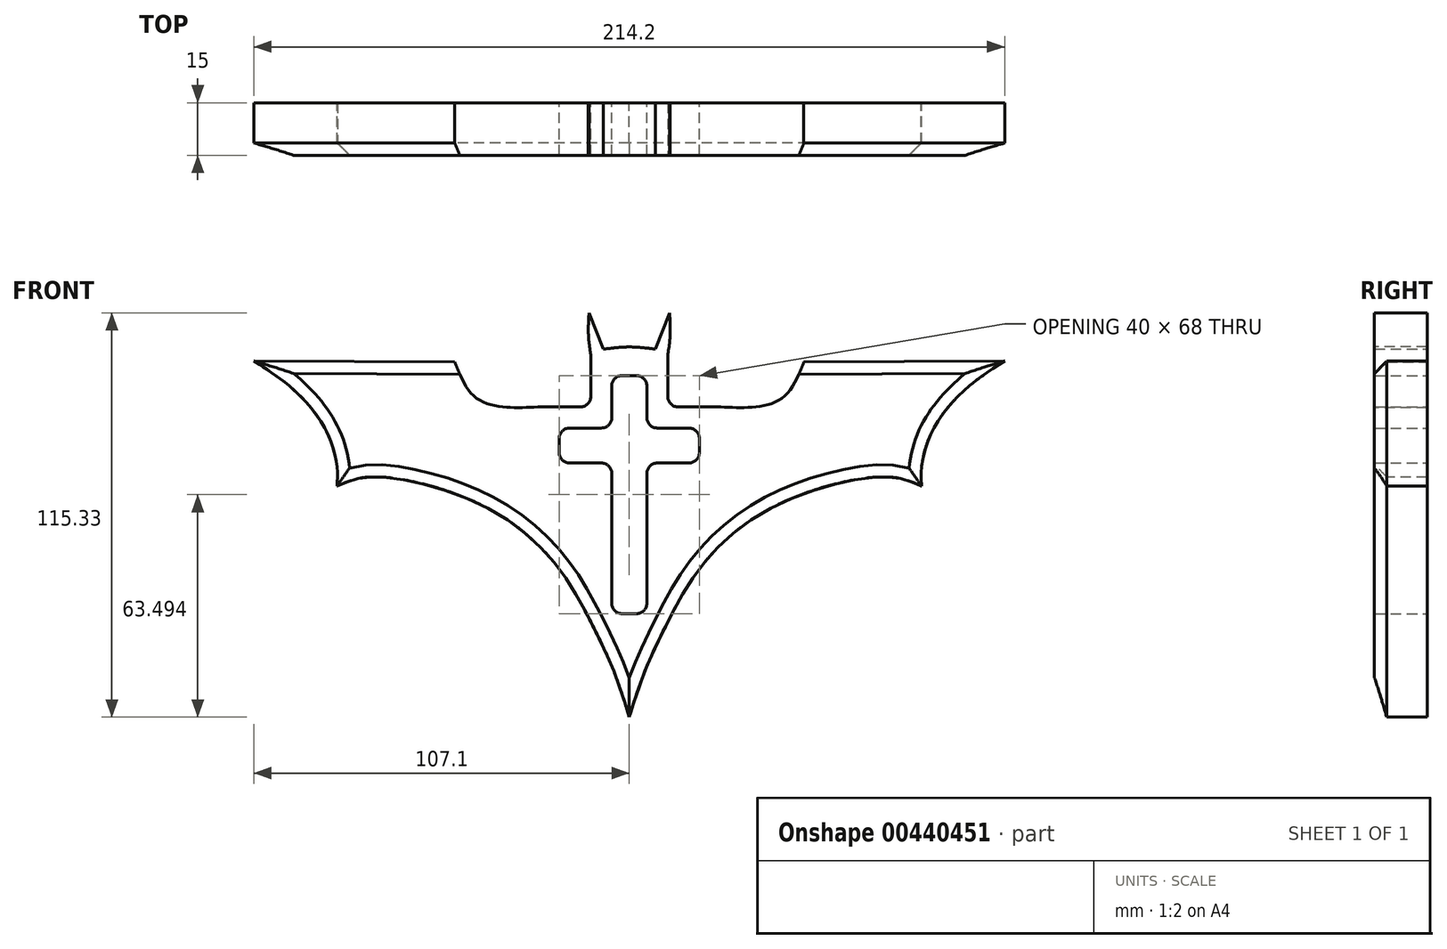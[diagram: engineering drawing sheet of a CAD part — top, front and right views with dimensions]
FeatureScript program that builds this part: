
annotation { "Feature Type Name" : "Feature", "Feature Type Description" : "" }
export const myFeature = defineFeature(function(context is Context, id is Id, definition is map)
    precondition{}
    {
        {
            var Q0;
            Q0=qCreatedBy(makeId("Front.planeOp"),FACE);
            var sketch = newSketch(context, id + "F0", { "sketchPlane" : qUnion([Q0])});
            skLineSegment(sketch, "E0", {"start": v(0, 58.13) * mm, "end": v(-10, 58.13) * mm});
            skLineSegment(sketch, "E1", {"start": v(-10, 58.13) * mm, "end": v(-10, 43.13) * mm});
            skLineSegment(sketch, "E2", {"start": v(-10, 43.13) * mm, "end": v(-25, 43.13) * mm});
            skLineSegment(sketch, "E3", {"start": v(-25, 43.13) * mm, "end": v(-25, 33.13) * mm});
            skLineSegment(sketch, "E4", {"start": v(-25, 33.13) * mm, "end": v(-10, 33.13) * mm});
            skLineSegment(sketch, "E5", {"start": v(0, 43.13) * mm, "end": v(15, 43.13) * mm});
            skLineSegment(sketch, "E6", {"start": v(0, 33.13) * mm, "end": v(15, 33.13) * mm});
            skLineSegment(sketch, "E7", {"start": v(15, 43.13) * mm, "end": v(15, 33.13) * mm});
            skLineSegment(sketch, "E8", {"start": v(0, 58.13) * mm, "end": v(0, 43.13) * mm});
            skLineSegment(sketch, "E9", {"start": v(-25, 27.13) * mm, "end": v(-16, 27.13) * mm});
            skLineSegment(sketch, "E10", {"start": v(6, 27.13) * mm, "end": v(15, 27.13) * mm});
            skLineSegment(sketch, "E11", {"start": v(15, 27.13) * mm, "end": v(21, 27.13) * mm});
            skLineSegment(sketch, "E12", {"start": v(21, 49.13) * mm, "end": v(6, 49.13) * mm});
            skLineSegment(sketch, "E13", {"start": v(6, 49.13) * mm, "end": v(6, 64.13) * mm});
            skLineSegment(sketch, "E14", {"start": v(6, 64.13) * mm, "end": v(-16, 64.13) * mm});
            skLineSegment(sketch, "E15", {"start": v(-16, 64.13) * mm, "end": v(-16, 49.13) * mm});
            skLineSegment(sketch, "E16", {"start": v(-16, 49.13) * mm, "end": v(-31, 49.13) * mm});
            skLineSegment(sketch, "E17", {"start": v(-31, 27.13) * mm, "end": v(-25, 27.13) * mm});
            skLineSegment(sketch, "E18", {"start": v(-16, 64.13) * mm, "end": v(-5, 64.13) * mm});
            skLineSegment(sketch, "E19", {"start": v(-5, 64.13) * mm, "end": v(-5, -22.87) * mm, "construction": true});
            skLineSegment(sketch, "E20", {"start": v(-31, 49.13) * mm, "end": v(-31, 27.13) * mm});
            skLineSegment(sketch, "E21", {"start": v(21, 49.13) * mm, "end": v(21, 27.13) * mm});
            skPoint(sketch, "E22", {"position": v(-88.4, 26.55) * mm});
            skFitSpline(sketch, "E23", {"points": [v(-31, 49.13) * mm, v(-40.4, 49.13) * mm, v(-49.1, 52.05) * mm, v(-54.8, 61.95) * mm], "startDerivative": vector(-28.83, -1.26) * mm, "endDerivative": vector(-12.96, 32.34) * mm});
            skPoint(sketch, "E24", {"position": v(-112.1, 62.25) * mm});
            skLineSegment(sketch, "E25", {"start": v(-54.8, 61.95) * mm, "end": v(-112.1, 62.25) * mm});
            skFitSpline(sketch, "E26", {"points": [v(-112.1, 62.25) * mm, v(-101.9, 55.05) * mm, v(-92, 43.35) * mm, v(-88.4, 32.25) * mm, v(-88.4, 26.55) * mm], "startDerivative": vector(38.34, -24.27) * mm, "endDerivative": vector(-2.08, -29.1) * mm});
            skFitSpline(sketch, "E27.MirrorCS", {"points": [v(102.1, 62.25) * mm, v(91.9, 55.05) * mm, v(82, 43.35) * mm, v(78.4, 32.25) * mm, v(78.4, 26.55) * mm], "startDerivative": vector(-38.34, -24.27) * mm, "endDerivative": vector(2.08, -29.1) * mm});
            skLineSegment(sketch, "E28.MirrorCS", {"start": v(44.8, 61.95) * mm, "end": v(102.1, 62.25) * mm});
            skFitSpline(sketch, "E29.MirrorCS", {"points": [v(21, 49.13) * mm, v(30.4, 49.13) * mm, v(39.1, 52.05) * mm, v(44.8, 61.95) * mm], "startDerivative": vector(28.83, -1.26) * mm, "endDerivative": vector(12.96, 32.34) * mm});
            skFitSpline(sketch, "E30", {"points": [v(-16, 64.13) * mm, v(-16.66, 69.78) * mm, v(-16.5, 75.97) * mm], "startDerivative": vector(-1.76, 11.4) * mm, "endDerivative": vector(0.76, 12.27) * mm});
            skFitSpline(sketch, "E31", {"points": [v(-16.5, 75.97) * mm, v(-11.82, 64.13) * mm], "startDerivative": vector(4.67, -11.83) * mm, "endDerivative": vector(4.67, -11.83) * mm});
            skFitSpline(sketch, "E32.MirrorCS", {"points": [v(6.5, 75.97) * mm, v(1.82, 64.13) * mm], "startDerivative": vector(-4.67, -11.83) * mm, "endDerivative": vector(-4.67, -11.83) * mm});
            skFitSpline(sketch, "E33.MirrorCS", {"points": [v(6, 64.13) * mm, v(6.66, 69.78) * mm, v(6.5, 75.97) * mm], "startDerivative": vector(1.76, 11.4) * mm, "endDerivative": vector(-0.76, 12.27) * mm});
            skLineSegment(sketch, "E34", {"start": v(-5, 64.13) * mm, "end": v(-5, 71.97) * mm});
            skFitSpline(sketch, "E35", {"points": [v(-12.41, 65.64) * mm, v(-5, 66.28) * mm, v(2.42, 65.66) * mm], "startDerivative": vector(14.83, 1.9) * mm, "endDerivative": vector(14.84, -1.87) * mm});
            skFitSpline(sketch, "E36", {"points": [v(-88.4, 26.55) * mm, v(-82.06, 28.79) * mm, v(-68.9, 28.3) * mm, v(-43.7, 19.35) * mm, v(-25.4, 3.45) * mm, v(-16, -12.15) * mm, v(-9.51, -26.08) * mm, v(-5, -39.36) * mm], "startDerivative": vector(63.66, 28.97) * mm, "endDerivative": vector(31.2, -100.4) * mm});
            skFitSpline(sketch, "E37.MirrorCS", {"points": [v(78.4, 26.55) * mm, v(72.06, 28.79) * mm, v(58.9, 28.3) * mm, v(33.7, 19.35) * mm, v(15.4, 3.45) * mm, v(6, -12.15) * mm, v(-0.49, -26.08) * mm, v(-5, -39.36) * mm], "startDerivative": vector(-63.66, 28.97) * mm, "endDerivative": vector(-31.2, -100.4) * mm});
            skLineSegment(sketch, "E38", {"start": v(-10, 33.13) * mm, "end": v(-10, -9.87) * mm});
            skLineSegment(sketch, "E39", {"start": v(0, 33.13) * mm, "end": v(0, -9.87) * mm});
            skLineSegment(sketch, "E40", {"start": v(0, -9.87) * mm, "end": v(-10, -9.87) * mm});
            skSolve(sketch);
        }
        {
            var Q0;
            Q0=qSketchRegion(id+"F0",true);
            extrude(context, id + "F1", {"entities" : qUnion([Q0]), "depth" : 15 * mm});
        }
        {
            var Q0;
            Q0=makeQuery(id+"F1.opExtrude","SWEPT_EDGE",EDGE,{"disambiguationData":[OSD([sQuery(id+"F0.wireOp",EDGE,"4Oll8tD9-mwlA-ZovC-NDif-auas1dVXo6qN"),sQuery(id+"F0.wireOp",EDGE,"aQmIDw4u-1cGP-j60T-XFLv-3MeWjV2oEF67"),sQuery(id+"F0.wireOp",EDGE,"SoNozwRW-mJtI-os8s-alWq-0gxmPMuzM5nE"),sQuery(id+"F0.wireOp",EDGE,"zj1N1qql-69xp-IFOC-AOg6-64gHm7Rjqr0n")])]});
            var Q1;
            Q1=makeQuery(id+"F1.opExtrude","SWEPT_EDGE",EDGE,{"disambiguationData":[OSD([sQuery(id+"F0.wireOp",EDGE,"E4"),sQuery(id+"F0.wireOp",EDGE,"aQmIDw4u-1cGP-j60T-XFLv-3MeWjV2oEF67")])]});
            var Q2;
            Q2=makeQuery(id+"F1.opExtrude","SWEPT_EDGE",EDGE,{"disambiguationData":[OSD([sQuery(id+"F0.wireOp",EDGE,"E3"),sQuery(id+"F0.wireOp",EDGE,"E4"),sQuery(id+"F0.wireOp",EDGE,"JkkYBlIC-WK7h-VhNU-eD4w-PFI7T7pZ055c")])]});
            var Q3;
            Q3=makeQuery(id+"F1.opExtrude","SWEPT_EDGE",EDGE,{"disambiguationData":[OSD([sQuery(id+"F0.wireOp",EDGE,"4Oll8tD9-mwlA-ZovC-NDif-auas1dVXo6qN"),sQuery(id+"F0.wireOp",EDGE,"2CsY11Ju-ztve-0Vkp-nJcy-8Y5b0dSNdEDy"),sQuery(id+"F0.wireOp",EDGE,"p5YPYbok-UCxx-zQt2-bGdL-7y8e1GDendUJ"),sQuery(id+"F0.wireOp",EDGE,"QCRdUmlX-UTfE-SmZh-7q9e-hv5Va6i25oJJ")])]});
            var Q4;
            Q4=makeQuery(id+"F1.opExtrude","SWEPT_EDGE",EDGE,{"disambiguationData":[OSD([sQuery(id+"F0.wireOp",EDGE,"E6"),sQuery(id+"F0.wireOp",EDGE,"2CsY11Ju-ztve-0Vkp-nJcy-8Y5b0dSNdEDy")])]});
            var Q5;
            Q5=makeQuery(id+"F1.opExtrude","SWEPT_EDGE",EDGE,{"disambiguationData":[OSD([sQuery(id+"F0.wireOp",EDGE,"E6"),sQuery(id+"F0.wireOp",EDGE,"E7"),sQuery(id+"F0.wireOp",EDGE,"M5XVuVZv-HyxV-EBHI-0UWz-zm9aioapNkRY"),sQuery(id+"F0.wireOp",EDGE,"HJXAKwE1-8RYy-Ky9X-1OAD-b5Pzt5JmRXUv")])]});
            var Q6;
            Q6=makeQuery(id+"F1.opExtrude","SWEPT_EDGE",EDGE,{"disambiguationData":[OSD([sQuery(id+"F0.wireOp",EDGE,"E5"),sQuery(id+"F0.wireOp",EDGE,"E7"),sQuery(id+"F0.wireOp",EDGE,"t1L3Ds75-5ZQ1-6rzq-zuNa-BfBlgHZkFqex"),sQuery(id+"F0.wireOp",EDGE,"EY3CKX2p-qQSQ-HcfL-y7fS-CjnnHh3G8Awt")])]});
            var Q7;
            Q7=makeQuery(id+"F1.opExtrude","SWEPT_EDGE",EDGE,{"disambiguationData":[OSD([sQuery(id+"F0.wireOp",EDGE,"E5"),sQuery(id+"F0.wireOp",EDGE,"E8")])]});
            var Q8;
            Q8=makeQuery(id+"F1.opExtrude","SWEPT_EDGE",EDGE,{"disambiguationData":[OSD([sQuery(id+"F0.wireOp",EDGE,"E0"),sQuery(id+"F0.wireOp",EDGE,"E8")])]});
            var Q9;
            Q9=makeQuery(id+"F1.opExtrude","SWEPT_EDGE",EDGE,{"disambiguationData":[OSD([sQuery(id+"F0.wireOp",EDGE,"E0"),sQuery(id+"F0.wireOp",EDGE,"E1")])]});
            var Q10;
            Q10=makeQuery(id+"F1.opExtrude","SWEPT_EDGE",EDGE,{"disambiguationData":[OSD([sQuery(id+"F0.wireOp",EDGE,"E1"),sQuery(id+"F0.wireOp",EDGE,"E2")])]});
            var Q11;
            Q11=makeQuery(id+"F1.opExtrude","SWEPT_EDGE",EDGE,{"disambiguationData":[OSD([sQuery(id+"F0.wireOp",EDGE,"E2"),sQuery(id+"F0.wireOp",EDGE,"E3")])]});
            fillet(context, id + "F2", {"entities" : qUnion([Q0, Q1, Q2, Q3, Q4, Q5, Q6, Q7, Q8, Q9, Q10, Q11]), "radius" : 3 * mm, "tangentPropagation" : true, "allowEdgeOverflow" : false});
        }
        {
            var Q0;
            Q0=makeQuery(id+"F1.opExtrude","SWEPT_EDGE",EDGE,{"disambiguationData":[OSD([sQuery(id+"F0.wireOp",EDGE,"E12"),sQuery(id+"F0.wireOp",EDGE,"E13")])]});
            fillet(context, id + "F3", {"entities" : qUnion([Q0]), "radius" : 3 * mm, "tangentPropagation" : true, "allowEdgeOverflow" : false});
        }
        {
            var Q0;
            Q0=makeQuery(id+"F1.opExtrude","SWEPT_EDGE",EDGE,{"disambiguationData":[OSD([sQuery(id+"F0.wireOp",EDGE,"E13"),sQuery(id+"F0.wireOp",EDGE,"E14")])]});
            var Q1;
            Q1=makeQuery(id+"F1.opExtrude","SWEPT_EDGE",EDGE,{"disambiguationData":[OSD([sQuery(id+"F0.wireOp",EDGE,"E14"),sQuery(id+"F0.wireOp",EDGE,"bEHc5zTc-oPVn-L3mY-NtSF-EzYglNQduDXi")])]});
            var Q2;
            Q2=makeQuery(id+"F1.opExtrude","SWEPT_EDGE",EDGE,{"disambiguationData":[OSD([sQuery(id+"F0.wireOp",EDGE,"sMuBDEL5-hzGn-YPGm-qX1Y-40NOGYWRmCt9"),sQuery(id+"F0.wireOp",EDGE,"E12")])]});
            var Q3;
            Q3=makeQuery(id+"F1.opExtrude","SWEPT_EDGE",EDGE,{"disambiguationData":[OSD([sQuery(id+"F0.wireOp",EDGE,"E11"),sQuery(id+"F0.wireOp",EDGE,"sMuBDEL5-hzGn-YPGm-qX1Y-40NOGYWRmCt9")])]});
            var Q4;
            Q4=makeQuery(id+"F1.opExtrude","SWEPT_EDGE",EDGE,{"disambiguationData":[OSD([sQuery(id+"F0.wireOp",EDGE,"56c6SDo8-Flvl-9hqR-lFgV-w5nGaxQKbkLZ"),sQuery(id+"F0.wireOp",EDGE,"E10")])]});
            var Q5;
            Q5=makeQuery(id+"F1.opExtrude","SWEPT_EDGE",EDGE,{"disambiguationData":[OSD([sQuery(id+"F0.wireOp",EDGE,"up3S4q3T-6OKs-mPOe-ITPR-dfA4uhlSpZ9u"),sQuery(id+"F0.wireOp",EDGE,"56c6SDo8-Flvl-9hqR-lFgV-w5nGaxQKbkLZ")])]});
            var Q6;
            Q6=makeQuery(id+"F1.opExtrude","SWEPT_EDGE",EDGE,{"disambiguationData":[OSD([sQuery(id+"F0.wireOp",EDGE,"K5r9tmWd-GK5V-TxqW-TA1t-Smk0NO8BXL6t"),sQuery(id+"F0.wireOp",EDGE,"up3S4q3T-6OKs-mPOe-ITPR-dfA4uhlSpZ9u")])]});
            var Q7;
            Q7=makeQuery(id+"F1.opExtrude","SWEPT_EDGE",EDGE,{"disambiguationData":[OSD([sQuery(id+"F0.wireOp",EDGE,"E9"),sQuery(id+"F0.wireOp",EDGE,"KHiQ8mEm-tS8j-iP5g-ifgn-kmPqBA0zGWJd")])]});
            var Q8;
            Q8=makeQuery(id+"F1.opExtrude","SWEPT_EDGE",EDGE,{"disambiguationData":[OSD([sQuery(id+"F0.wireOp",EDGE,"2tCYhLwo-kV1n-wEjR-YmM0-9tpOZI8bn5kh"),sQuery(id+"F0.wireOp",EDGE,"E17")])]});
            var Q9;
            Q9=makeQuery(id+"F1.opExtrude","SWEPT_EDGE",EDGE,{"disambiguationData":[OSD([sQuery(id+"F0.wireOp",EDGE,"E16"),sQuery(id+"F0.wireOp",EDGE,"2tCYhLwo-kV1n-wEjR-YmM0-9tpOZI8bn5kh")])]});
            var Q10;
            Q10=makeQuery(id+"F1.opExtrude","SWEPT_EDGE",EDGE,{"disambiguationData":[OSD([sQuery(id+"F0.wireOp",EDGE,"E18"),sQuery(id+"F0.wireOp",EDGE,"bEHc5zTc-oPVn-L3mY-NtSF-EzYglNQduDXi")])]});
            var Q11;
            Q11=makeQuery(id+"F1.opExtrude","SWEPT_EDGE",EDGE,{"disambiguationData":[OSD([sQuery(id+"F0.wireOp",EDGE,"E15"),sQuery(id+"F0.wireOp",EDGE,"E18")])]});
            var Q12;
            Q12=makeQuery(id+"F1.opExtrude","SWEPT_EDGE",EDGE,{"disambiguationData":[OSD([sQuery(id+"F0.wireOp",EDGE,"E15"),sQuery(id+"F0.wireOp",EDGE,"E16")])]});
            fillet(context, id + "F4", {"entities" : qUnion([Q0, Q1, Q2, Q3, Q4, Q5, Q6, Q7, Q8, Q9, Q10, Q11, Q12]), "radius" : 3 * mm, "tangentPropagation" : true, "allowEdgeOverflow" : false});
        }
        {
            var Q0;
            Q0=makeQuery(id+"F1.opExtrude","CAP_EDGE",EDGE,{"disambiguationData":[OSD([sQuery(id+"F0.wireOp",EDGE,"E26")])],"isStart":false});
            var Q1;
            Q1=makeQuery(id+"F1.opExtrude","CAP_EDGE",EDGE,{"disambiguationData":[OSD([sQuery(id+"F0.wireOp",EDGE,"c2d85f96-0120-477e-80eb-17426db88d95")])],"isStart":false});
            var Q2;
            Q2=makeQuery(id+"F1.opExtrude","CAP_EDGE",EDGE,{"disambiguationData":[OSD([sQuery(id+"F0.wireOp",EDGE,"0bd430e7-d675-4036-86b9-4377e7417ed40.MirrorCS")])],"isStart":false});
            var Q3;
            Q3=makeQuery(id+"F1.opExtrude","CAP_EDGE",EDGE,{"disambiguationData":[OSD([sQuery(id+"F0.wireOp",EDGE,"E27.MirrorCS")])],"isStart":false});
            var Q4;
            Q4=makeQuery(id+"F1.opExtrude","CAP_EDGE",EDGE,{"disambiguationData":[OSD([sQuery(id+"F0.wireOp",EDGE,"E28.MirrorCS")])],"isStart":false});
            var Q5;
            Q5=makeQuery(id+"F1.opExtrude","CAP_EDGE",EDGE,{"disambiguationData":[OSD([sQuery(id+"F0.wireOp",EDGE,"E36")])],"isStart":false});
            var Q6;
            Q6=makeQuery(id+"F1.opExtrude","CAP_EDGE",EDGE,{"disambiguationData":[OSD([sQuery(id+"F0.wireOp",EDGE,"E37.MirrorCS")])],"isStart":false});
            chamfer(context, id + "F5", {"entities" : qUnion([Q0, Q1, Q2, Q3, Q4, Q5, Q6]), "width" : 3.5 * mm, "tangentPropagation" : true});
        }
        {
            var Q0;
            Q0=makeQuery(id+"F1.opExtrude","CAP_EDGE",EDGE,{"disambiguationData":[OSD([sQuery(id+"F0.wireOp",EDGE,"E25")])],"isStart":false});
            chamfer(context, id + "F6", {"entities" : qUnion([Q0]), "width" : 3.5 * mm, "tangentPropagation" : true});
        }
        {
            var Q0;
            Q0=makeQuery(id+"F1.opExtrude","SWEPT_EDGE",EDGE,{"disambiguationData":[OSD([sQuery(id+"F0.wireOp",EDGE,"E38"),sQuery(id+"F0.wireOp",EDGE,"E40")])]});
            var Q1;
            Q1=makeQuery(id+"F1.opExtrude","SWEPT_EDGE",EDGE,{"disambiguationData":[OSD([sQuery(id+"F0.wireOp",EDGE,"E39"),sQuery(id+"F0.wireOp",EDGE,"E40")])]});
            fillet(context, id + "F7", {"entities" : qUnion([Q0, Q1]), "radius" : 3 * mm, "tangentPropagation" : true, "allowEdgeOverflow" : false});
        }
    });
